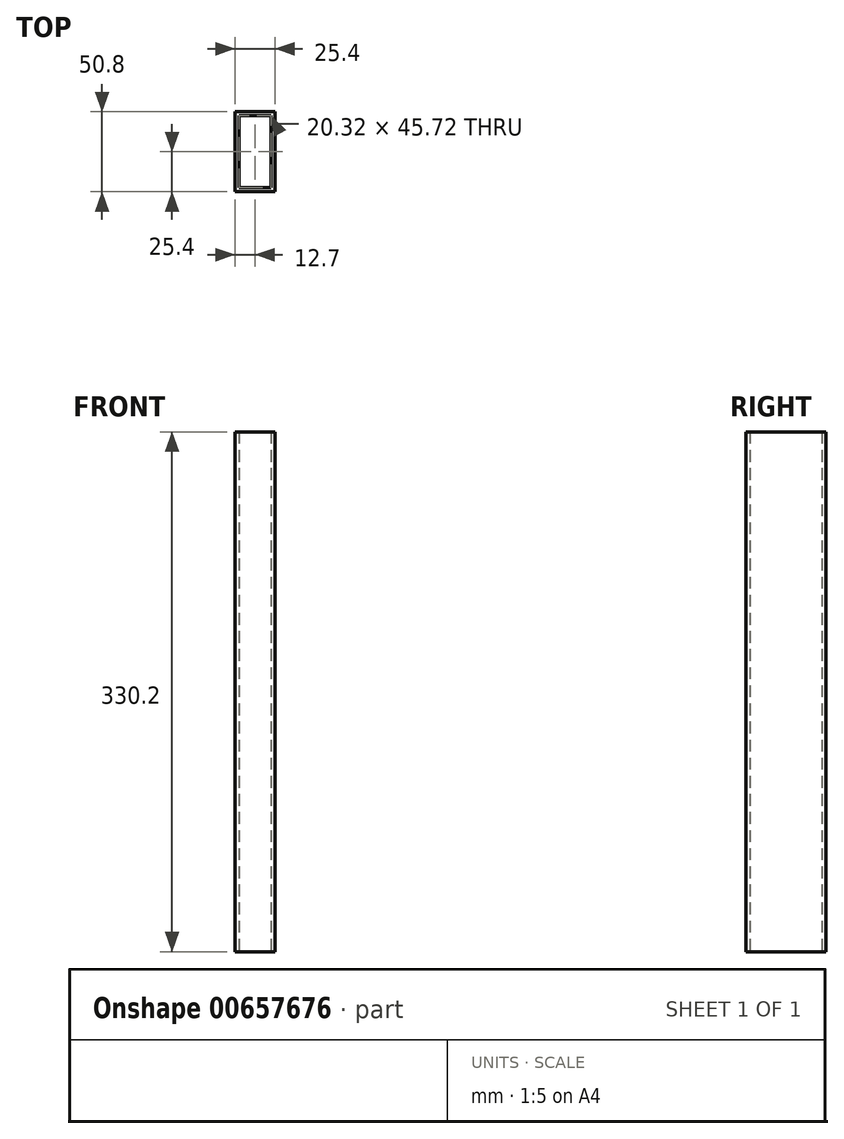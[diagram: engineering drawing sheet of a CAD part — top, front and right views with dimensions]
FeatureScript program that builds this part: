
annotation { "Feature Type Name" : "Feature", "Feature Type Description" : "" }
export const myFeature = defineFeature(function(context is Context, id is Id, definition is map)
    precondition{}
    {
        {
            var Q0;
            Q0=qCreatedBy(makeId("Top.planeOp"),FACE);
            var sketch = newSketch(context, id + "F0", { "sketchPlane" : qUnion([Q0])});
            skLineSegment(sketch, "E0.bottom", {"start": v(0, 0) * mm, "end": v(25.4, 0) * mm});
            skLineSegment(sketch, "E0.top", {"start": v(0, -50.8) * mm, "end": v(25.4, -50.8) * mm});
            skLineSegment(sketch, "E0.left", {"start": v(0, 0) * mm, "end": v(0, -50.8) * mm});
            skLineSegment(sketch, "E0.right", {"start": v(25.4, 0) * mm, "end": v(25.4, -50.8) * mm});
            skLineSegment(sketch, "E1.bottom", {"start": v(2.54, -48.26) * mm, "end": v(22.86, -48.26) * mm});
            skLineSegment(sketch, "E1.top", {"start": v(2.54, -2.54) * mm, "end": v(22.86, -2.54) * mm});
            skLineSegment(sketch, "E1.left", {"start": v(2.54, -48.26) * mm, "end": v(2.54, -2.54) * mm});
            skLineSegment(sketch, "E1.right", {"start": v(22.86, -48.26) * mm, "end": v(22.86, -2.54) * mm});
            skSolve(sketch);
        }
        {
            var Q0;
            Q0=makeQuery(id+"F0.imprint","IMPRINT",FACE,{"disambiguationData":[TD([[makeQuery(id+"F0.imprint","IMPRINT",EDGE,{"derivedFrom":sQuery(id+"F0.wireOp",EDGE,"E0.bottom")}),-1.0]])]});
            extrude(context, id + "F1", {"entities" : qUnion([Q0]), "depth" : 330.2 * mm, "offsetDistance" : 25.4 * mm});
        }
    });
